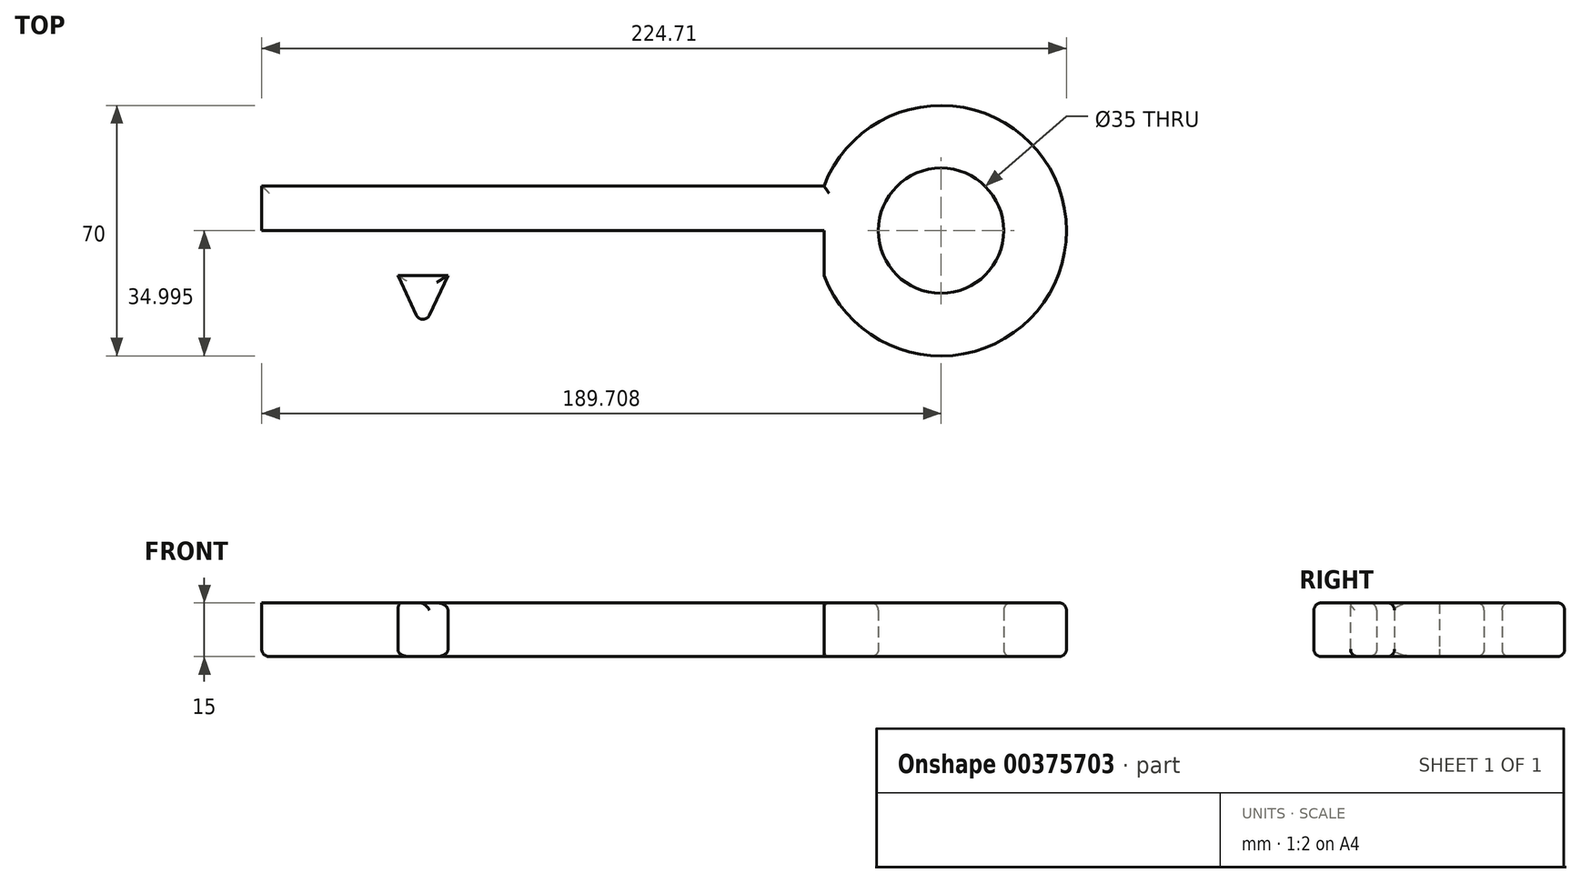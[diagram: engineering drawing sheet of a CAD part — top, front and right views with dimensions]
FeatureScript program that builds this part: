
annotation { "Feature Type Name" : "Feature", "Feature Type Description" : "" }
export const myFeature = defineFeature(function(context is Context, id is Id, definition is map)
    precondition{}
    {
        {
            var Q0;
            Q0=qCreatedBy(makeId("Top.planeOp"),FACE);
            var sketch = newSketch(context, id + "F0", { "sketchPlane" : qUnion([Q0])});
            skLineSegment(sketch, "E0.bottom", {"start": v(-95.59, 16.67) * mm, "end": v(61.43, 16.67) * mm});
            skLineSegment(sketch, "E0.top", {"start": v(-95.59, -8.33) * mm, "end": v(61.43, -8.33) * mm});
            skLineSegment(sketch, "E0.left", {"start": v(-95.59, 16.67) * mm, "end": v(-95.59, -8.33) * mm});
            skLineSegment(sketch, "E0.right", {"start": v(61.43, 16.67) * mm, "end": v(61.43, -8.33) * mm});
            skLineSegment(sketch, "E1.bottom", {"start": v(-95.59, -8.33) * mm, "end": v(-85.59, -8.33) * mm});
            skLineSegment(sketch, "E1.top", {"start": v(-95.59, -38.33) * mm, "end": v(-85.59, -38.33) * mm});
            skLineSegment(sketch, "E1.left", {"start": v(-95.59, -8.33) * mm, "end": v(-95.59, -38.33) * mm});
            skLineSegment(sketch, "E1.right", {"start": v(-85.59, -8.33) * mm, "end": v(-85.59, -38.33) * mm});
            skLineSegment(sketch, "E2.bottom", {"start": v(-75.59, -8.33) * mm, "end": v(-67.59, -8.33) * mm});
            skLineSegment(sketch, "E2.top", {"start": v(-75.59, -23.33) * mm, "end": v(-67.59, -23.33) * mm});
            skLineSegment(sketch, "E2.left", {"start": v(-75.59, -8.33) * mm, "end": v(-75.59, -23.33) * mm});
            skLineSegment(sketch, "E2.right", {"start": v(-67.59, -8.33) * mm, "end": v(-67.59, -23.33) * mm});
            skLineSegment(sketch, "E3", {"start": v(-57.59, -8.33) * mm, "end": v(-50.59, -23.33) * mm});
            skLineSegment(sketch, "E4", {"start": v(-43.59, -8.33) * mm, "end": v(-50.59, -23.33) * mm});
            skArc(sketch, "E5", {"start": v(61.43, -8.33) * mm, "mid": v(129.12, 4.17) * mm, "end": v(61.43, 16.67) * mm});
            skCircle(sketch, "E6", {"center": v(94.12, 4.17) * mm, "radius": 17.5 * mm});
            skLineSegment(sketch, "E7", {"start": v(94.12, 4.17) * mm, "end": v(-95.59, 4.17) * mm});
            skSolve(sketch);
        }
        {
            var Q0;
            {var subQ0=sQuery(id+"F0.wireOp",EDGE,"E3");Q0=makeQuery(id+"F0.imprint","IMPRINT",FACE,{"disambiguationData":[TD([[makeQuery(id+"F0.imprint","IMPRINT",EDGE,{"derivedFrom":subQ0}),1.0]])]});}
            var Q1;
            Q1=makeQuery(id+"F0.imprint","IMPRINT",FACE,{"disambiguationData":[TD([[makeQuery(id+"F0.imprint","IMPRINT",EDGE,{"derivedFrom":sQuery(id+"F0.wireOp",EDGE,"E1.bottom")}),-1.0]])]});
            var Q2;
            Q2=makeQuery(id+"F0.imprint","IMPRINT",FACE,{"disambiguationData":[TD([[makeQuery(id+"F0.imprint","IMPRINT",EDGE,{"derivedFrom":sQuery(id+"F0.wireOp",EDGE,"E2.bottom")}),-1.0]])]});
            var Q3;
            {var subQ0=sQuery(id+"F0.wireOp",EDGE,"E0.bottom");Q3=makeQuery(id+"F0.imprint","IMPRINT",FACE,{"disambiguationData":[TD([[makeQuery(id+"F0.imprint","IMPRINT",EDGE,{"derivedFrom":subQ0}),-1.0]])]});}
            var Q4;
            {var subQ6=sQuery(id+"F0.wireOp",EDGE,"E1.bottom");Q4=makeQuery(id+"F0.imprint","IMPRINT",FACE,{"disambiguationData":[TD([[makeQuery(id+"F0.imprint","IMPRINT",EDGE,{"derivedFrom":subQ6}),1.0]])]});}
            var Q5;
            {var subQ0=sQuery(id+"F0.wireOp",EDGE,"E5");Q5=makeQuery(id+"F0.imprint","IMPRINT",FACE,{"disambiguationData":[TD([[makeQuery(id+"F0.imprint","IMPRINT",EDGE,{"derivedFrom":subQ0}),1.0]])]});}
            extrude(context, id + "F1", {"entities" : qUnion([Q0, Q1, Q2, Q3, Q4, Q5]), "depth" : 15 * mm});
        }
        {
            var Q0;
            Q0=makeQuery(id+"F1.opExtrude","CAP_EDGE",EDGE,{"disambiguationData":[OSD([sQuery(id+"F0.wireOp",EDGE,"E5")])],"isStart":false});
            var Q1;
            Q1=makeQuery(id+"F1.opExtrude","CAP_EDGE",EDGE,{"disambiguationData":[OSD([sQuery(id+"F0.wireOp",EDGE,"E0.bottom")])],"isStart":false});
            var Q2;
            Q2=makeQuery(id+"F1.opExtrude","CAP_EDGE",EDGE,{"disambiguationData":[OSD([sQuery(id+"F0.wireOp",EDGE,"E4")])],"isStart":false});
            var Q3;
            Q3=makeQuery(id+"F1.opExtrude","CAP_EDGE",EDGE,{"disambiguationData":[OSD([sQuery(id+"F0.wireOp",EDGE,"E2.right")])],"isStart":false});
            var Q4;
            Q4=makeQuery(id+"F1.opExtrude","CAP_EDGE",EDGE,{"disambiguationData":[OSD([sQuery(id+"F0.wireOp",EDGE,"E1.right")])],"isStart":false});
            var Q5;
            Q5=makeQuery(id+"F1.opExtrude","CAP_EDGE",EDGE,{"disambiguationData":[OSD([sQuery(id+"F0.wireOp",EDGE,"E6")])],"isStart":true});
            var Q6;
            Q6=makeQuery(id+"F1.opExtrude","CAP_EDGE",EDGE,{"disambiguationData":[OSD([sQuery(id+"F0.wireOp",EDGE,"E6")])],"isStart":false});
            var Q7;
            Q7=makeQuery(id+"F1.opExtrude","CAP_EDGE",EDGE,{"disambiguationData":[OSD([sQuery(id+"F0.wireOp",EDGE,"E5")])],"isStart":true});
            var Q8;
            {var subQ0=sQuery(id+"F0.wireOp",EDGE,"E0.top");Q8=makeQuery(id+"F1.opExtrude","CAP_EDGE",EDGE,{"disambiguationData":[OSD([subQ0]),TDD([makeQuery(id+"F0.imprint","IMPRINT",EDGE,{"disambiguationData":[TD([[makeQuery(id+"F0.imprint","INTERSECT",VERTEX,{"derivedFrom":[subQ0,sQuery(id+"F0.wireOp",EDGE,"E4")]}),-1.0]])],"derivedFrom":subQ0})])],"isStart":true});}
            var Q9;
            Q9=makeQuery(id+"F1.opExtrude","CAP_EDGE",EDGE,{"disambiguationData":[OSD([sQuery(id+"F0.wireOp",EDGE,"E0.bottom")])],"isStart":true});
            var Q10;
            Q10=makeQuery(id+"F1.opExtrude","CAP_EDGE",EDGE,{"disambiguationData":[OSD([sQuery(id+"F0.wireOp",EDGE,"E3")])],"isStart":true});
            var Q11;
            Q11=makeQuery(id+"F1.opExtrude","SWEPT_EDGE",EDGE,{"disambiguationData":[OSD([sQuery(id+"F0.wireOp",EDGE,"E3"),sQuery(id+"F0.wireOp",EDGE,"E4")])]});
            var Q12;
            Q12=makeQuery(id+"F1.opExtrude","SWEPT_EDGE",EDGE,{"disambiguationData":[OSD([sQuery(id+"F0.wireOp",EDGE,"E2.top"),sQuery(id+"F0.wireOp",EDGE,"E2.right")])]});
            var Q13;
            Q13=makeQuery(id+"F1.opExtrude","CAP_EDGE",EDGE,{"disambiguationData":[OSD([sQuery(id+"F0.wireOp",EDGE,"E2.top")])],"isStart":true});
            var Q14;
            Q14=makeQuery(id+"F1.opExtrude","CAP_EDGE",EDGE,{"disambiguationData":[OSD([sQuery(id+"F0.wireOp",EDGE,"E2.left")])],"isStart":true});
            var Q15;
            Q15=makeQuery(id+"F1.opExtrude","CAP_EDGE",EDGE,{"disambiguationData":[OSD([sQuery(id+"F0.wireOp",EDGE,"E1.right")])],"isStart":true});
            var Q16;
            Q16=makeQuery(id+"F1.opExtrude","CAP_EDGE",EDGE,{"disambiguationData":[OSD([sQuery(id+"F0.wireOp",EDGE,"E0.left"),sQuery(id+"F0.wireOp",EDGE,"E1.left")])],"isStart":true});
            var Q17;
            Q17=makeQuery(id+"F1.opExtrude","CAP_FACE",FACE,{"disambiguationData":[OSD([sQuery(id+"F0.wireOp",EDGE,"E0.bottom"),sQuery(id+"F0.wireOp",EDGE,"E0.top"),sQuery(id+"F0.wireOp",EDGE,"E0.left"),sQuery(id+"F0.wireOp",EDGE,"E1.top"),sQuery(id+"F0.wireOp",EDGE,"E1.left"),sQuery(id+"F0.wireOp",EDGE,"E1.right"),sQuery(id+"F0.wireOp",EDGE,"E2.top"),sQuery(id+"F0.wireOp",EDGE,"E2.left"),sQuery(id+"F0.wireOp",EDGE,"E2.right"),sQuery(id+"F0.wireOp",EDGE,"E3"),sQuery(id+"F0.wireOp",EDGE,"E4"),sQuery(id+"F0.wireOp",EDGE,"E5"),sQuery(id+"F0.wireOp",EDGE,"E6")])],"isStart":true});
            var Q18;
            {var subQ0=sQuery(id+"F0.wireOp",EDGE,"E0.top");Q18=makeQuery(id+"F1.opExtrude","CAP_EDGE",EDGE,{"disambiguationData":[OSD([subQ0]),TDD([makeQuery(id+"F0.imprint","IMPRINT",EDGE,{"disambiguationData":[TD([[makeQuery(id+"F0.imprint","INTERSECT",VERTEX,{"derivedFrom":[subQ0,sQuery(id+"F0.wireOp",EDGE,"E4")]}),-1.0]])],"derivedFrom":subQ0})])],"isStart":false});}
            fillet(context, id + "F2", {"entities" : qUnion([Q0, Q1, Q2, Q3, Q4, Q5, Q6, Q7, Q8, Q9, Q10, Q11, Q12, Q13, Q14, Q15, Q16, Q17, Q18]), "radius" : 2 * mm, "tangentPropagation" : true, "allowEdgeOverflow" : false});
        }
    });
